# Revit family: Deca_Bacia Sanitária Convencional Cubo com Assento_P.26
name_source: partatom
category: Plumbing Fixtures
revit_build: Autodesk Revit Architecture 2012 (Build: 20120126_0600(x64)
units: mm (PartAtom-declared; Revit-internal decimal feet)

## types (4) — shared parameters
Acompanha o Produto = Anel de vedação (AV.90.01), tubo de ligação, conjunto de fixação SP.121.01, acabamento lateral, calço e assento em poliester.
Aprovado por = Contino/quattroD
Assembly Code = D2010110
Atendimento ao Cliente = 0800-0117073
Consumo = 6 lpf
Criado por = Contino/quattroD
Description = Bacia sanitária convencional
Diâmetro Ponto de Esgoto = 100 mm  [stored 0.328084 ft]
Diâmetro Água Fria = 40 mm  [stored 0.131234 ft]
Flow Pressure = 0.00 psi
Linha = Cubo
Louça/Metais = Louça
Manufacturer = Deca
Material = Deca_Vitreous China
Norma = ABNT NBR 15097-1: 2011
Peso Liquido (Kg) = 41
Pressão = 2 a 40 mca
Produto = Bacia sanitária convencional Cubo com assento
Raio Ponto de Esgoto = 50 mm  [stored 0.164042 ft]
Raio Água Fria = 20 mm  [stored 0.0656168 ft]
Segmento = Luxo
URL = www.deca.com.br/produtos
Variações de COR = Branco e fixação cromada (P.26C.17); Branco e fixação dourada (P.26D.17); Ébano e fixação cromada (P.26C.95); Ébano e fixação dourada (P.26D.95)
zero-valued in all types: CWFU, Default Elevation, WFU

## per-type parameters (varying)
| type | Assento | Bacia | Código | Model |
| P.26C.17_Branco Gelo GE17_Fixação Cromada | Deca GE17 Branco Gelo Poliéster | Deca GE17 Branco Gelo Cerâmica | P.26C.17 | P.26C.17 |
| P.26C.95_Ébano EB95_Fixação Cromada | Deca EB95 Ébano Poliéster | Deca EB95 Ébano Cerâmica | P.26C.95 | P.26C.95 |
| P.26D.95_Ébano EB95_Fixação Dourada | Deca EB95 Ébano Poliéster | Deca EB95 Ébano Cerâmica | P.26D.95 | P.26D.95 |
| P.26D.17_Branco Gelo GE17_Fixação Dourada | Deca GE17 Branco Gelo Poliéster | Deca GE17 Branco Gelo Cerâmica | P.26D.17 | P.26D.17 |

note: [stored X ft] marks values corroborated as IEEE doubles in the binary element streams (Revit-internal decimal feet)

## geometry (parser evidence)
native form markers: Blend x16, Sweep x1
no freeform markers — native parametric forms only
